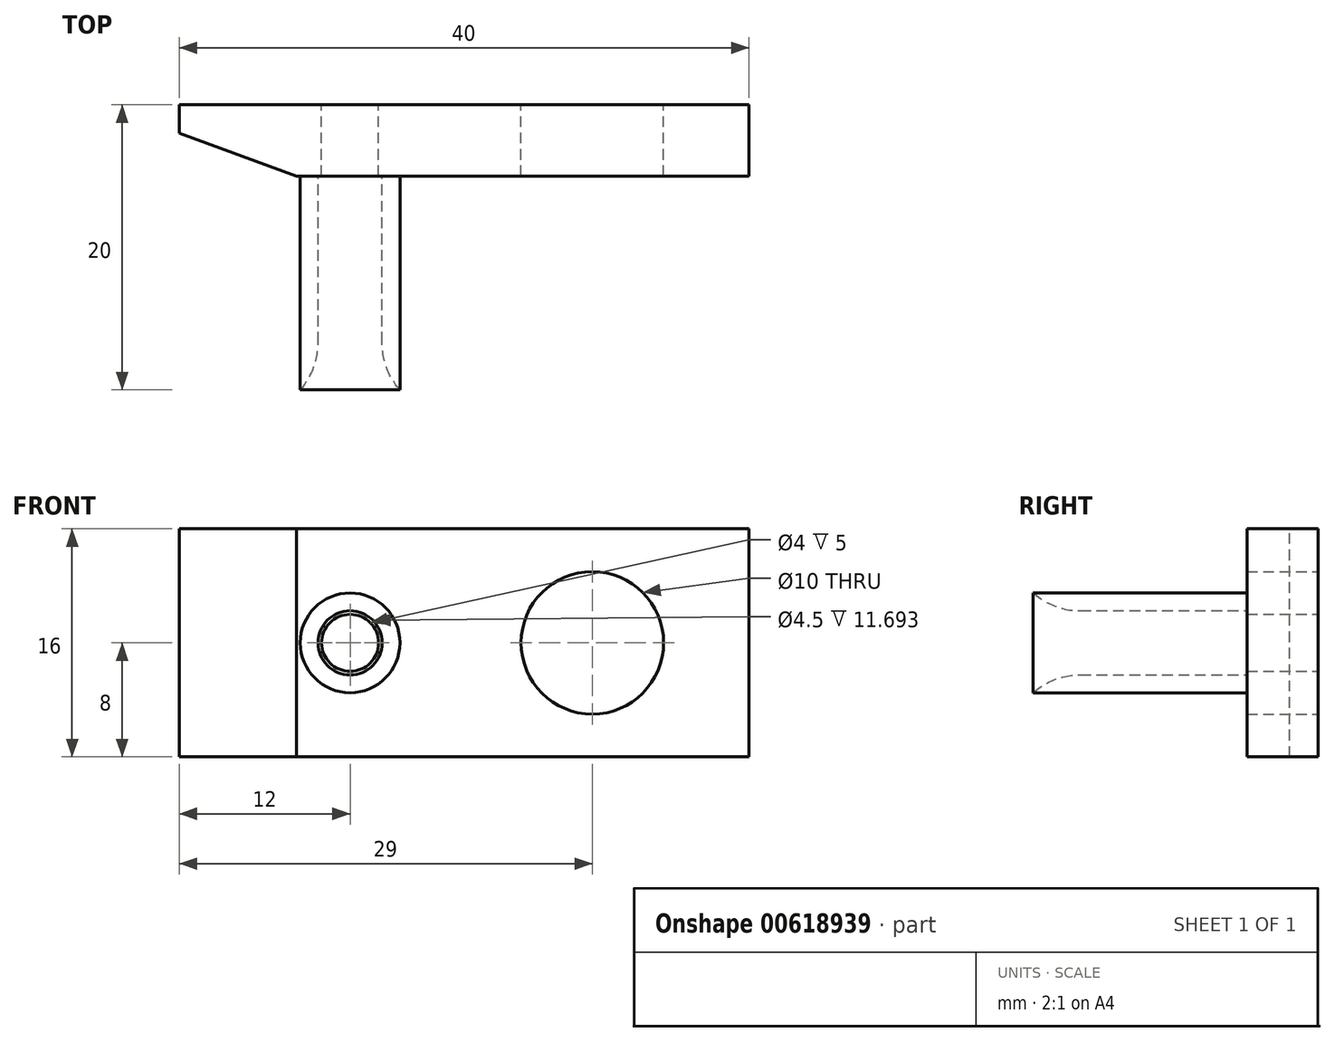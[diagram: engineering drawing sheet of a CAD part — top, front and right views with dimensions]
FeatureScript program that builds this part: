
annotation { "Feature Type Name" : "Feature", "Feature Type Description" : "" }
export const myFeature = defineFeature(function(context is Context, id is Id, definition is map)
    precondition{}
    {
        {
            var Q0;
            Q0=qCreatedBy(makeId("Front.planeOp"),FACE);
            var sketch = newSketch(context, id + "F0", { "sketchPlane" : qUnion([Q0])});
            skLineSegment(sketch, "E0.bottom", {"start": v(20, -8) * mm, "end": v(-20, -8) * mm});
            skLineSegment(sketch, "E0.top", {"start": v(20, 8) * mm, "end": v(-20, 8) * mm});
            skLineSegment(sketch, "E0.left", {"start": v(20, -8) * mm, "end": v(20, 8) * mm});
            skLineSegment(sketch, "E0.right", {"start": v(-20, -8) * mm, "end": v(-20, 8) * mm});
            skPoint(sketch, "E0.middle", {"position": v(0, 0) * mm});
            skLineSegment(sketch, "E1", {"start": v(20, 0) * mm, "end": v(9, 0) * mm});
            skPoint(sketch, "E1.endSnap0", {"position": v(20, 0) * mm});
            skCircle(sketch, "E2", {"center": v(9, 0) * mm, "radius": 5 * mm});
            skLineSegment(sketch, "E3", {"start": v(-20, 0) * mm, "end": v(-8, 0) * mm});
            skPoint(sketch, "E3.endSnap0", {"position": v(-20, 0) * mm});
            skCircle(sketch, "E4", {"center": v(-8, 0) * mm, "radius": 2 * mm});
            skSolve(sketch);
        }
        {
            var Q0;
            Q0 = qSketchRegion(id + "F0", true);
            extrude(context, id + "F1", {"entities" : qUnion([Q0]), "depth" : 5 * mm, "offsetDistance" : 25 * mm});
        }
        {
            var Q0;
            Q0=makeQuery(id+"F1.opExtrude","CAP_FACE",FACE,{"disambiguationData":[OSD([sQuery(id+"F0.wireOp",EDGE,"E0.bottom"),sQuery(id+"F0.wireOp",EDGE,"E0.top"),sQuery(id+"F0.wireOp",EDGE,"E0.left"),sQuery(id+"F0.wireOp",EDGE,"E0.right"),sQuery(id+"F0.wireOp",EDGE,"E2"),sQuery(id+"F0.wireOp",EDGE,"E4")])],"isStart":false});
            var sketch = newSketch(context, id + "F2", { "sketchPlane" : qUnion([Q0])});
            skCircle(sketch, "E5", {"center": v(-8, 0) * mm, "radius": 2.25 * mm});
            skCircle(sketch, "E6", {"center": v(-8, 0) * mm, "radius": 3.5 * mm});
            skSolve(sketch);
        }
        {
            var Q0;
            Q0 = qSketchRegion(id + "F2", true);
            extrude(context, id + "F3", {"entities" : qUnion([Q0]), "operationType" : NewBodyOperationType.ADD, "depth" : 15 * mm, "offsetDistance" : 25 * mm});
        }
        {
            var Q0;
            Q0=makeQuery(id+"F3.opExtrude","CAP_EDGE",EDGE,{"disambiguationData":[OSD([sQuery(id+"F2.wireOp",EDGE,"E5")])],"isStart":false});
            fillet(context, id + "F4", {"entities" : qUnion([Q0]), "radius" : 5 * mm, "tangentPropagation" : true, "allowEdgeOverflow" : false});
        }
        {
            var Q0;
            Q0=makeQuery(id+"F1.opExtrude","CAP_EDGE",EDGE,{"disambiguationData":[OSD([sQuery(id+"F0.wireOp",EDGE,"E0.right")])],"isStart":false});
            chamfer(context, id + "F5", {"entities" : qUnion([Q0]), "chamferType" : ChamferType.OFFSET_ANGLE, "width" : 3 * mm, "oppositeDirection" : false, "angle" : 70 * degree, "tangentPropagation" : true});
        }
    });
